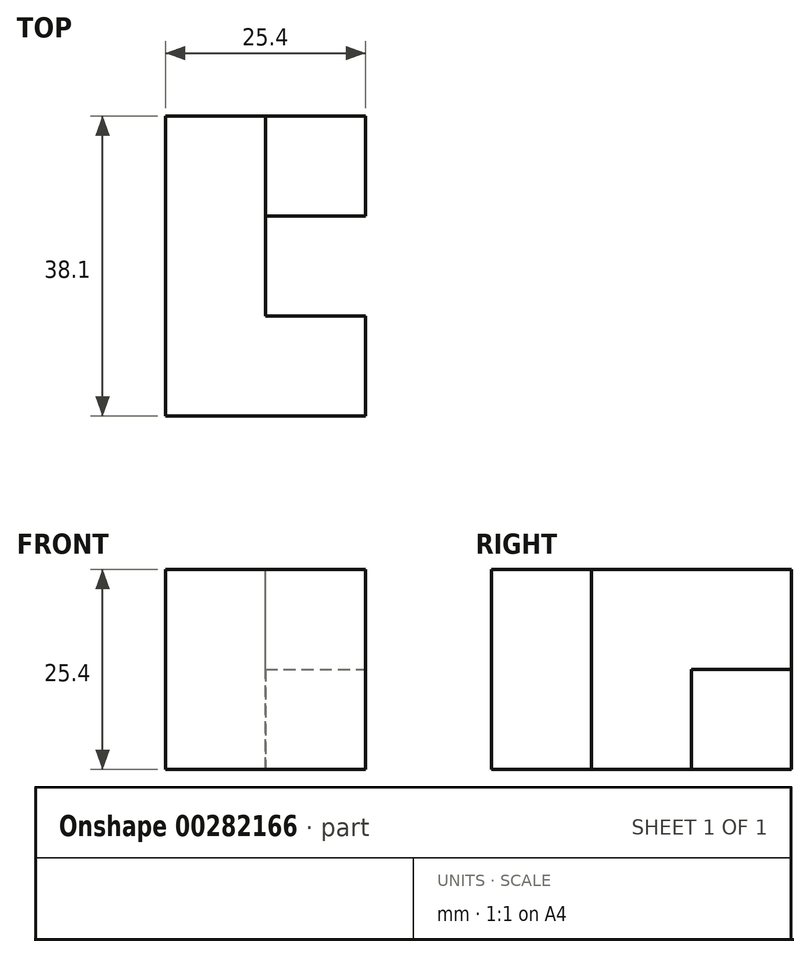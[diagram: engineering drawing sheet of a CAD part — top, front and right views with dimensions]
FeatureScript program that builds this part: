
annotation { "Feature Type Name" : "Feature", "Feature Type Description" : "" }
export const myFeature = defineFeature(function(context is Context, id is Id, definition is map)
    precondition{}
    {
        {
            var Q0;
            Q0=qCreatedBy(makeId("Right.planeOp"),FACE);
            var sketch = newSketch(context, id + "F0", { "sketchPlane" : qUnion([Q0])});
            skLineSegment(sketch, "E0.bottom", {"start": v(0, 0) * mm, "end": v(38.1, 0) * mm});
            skLineSegment(sketch, "E0.top", {"start": v(0, 25.4) * mm, "end": v(38.1, 25.4) * mm});
            skLineSegment(sketch, "E0.left", {"start": v(0, 0) * mm, "end": v(0, 25.4) * mm});
            skLineSegment(sketch, "E0.right", {"start": v(38.1, 0) * mm, "end": v(38.1, 25.4) * mm});
            skSolve(sketch);
        }
        {
            var Q0;
            Q0=makeQuery(id+"F0.imprint","IMPRINT",FACE,{"disambiguationData":[TD([[makeQuery(id+"F0.imprint","IMPRINT",EDGE,{"derivedFrom":sQuery(id+"F0.wireOp",EDGE,"E0.bottom")}),1.0]])]});
            extrude(context, id + "F1", {"entities" : qUnion([Q0]), "depth" : 25.4 * mm});
        }
        {
            var Q0;
            Q0=makeQuery(id+"F1.opExtrude","CAP_FACE",FACE,{"disambiguationData":[OSD([sQuery(id+"F0.wireOp",EDGE,"E0.bottom"),sQuery(id+"F0.wireOp",EDGE,"E0.top"),sQuery(id+"F0.wireOp",EDGE,"E0.left"),sQuery(id+"F0.wireOp",EDGE,"E0.right")])],"isStart":false});
            var sketch = newSketch(context, id + "F2", { "sketchPlane" : qUnion([Q0])});
            skLineSegment(sketch, "E1", {"start": v(25.4, 0) * mm, "end": v(12.7, 0) * mm});
            skLineSegment(sketch, "E2", {"start": v(12.7, 0) * mm, "end": v(12.7, 25.4) * mm});
            skLineSegment(sketch, "E3", {"start": v(12.7, 25.4) * mm, "end": v(38.1, 25.4) * mm});
            skLineSegment(sketch, "E4", {"start": v(38.1, 25.4) * mm, "end": v(38.1, 12.7) * mm});
            skLineSegment(sketch, "E5", {"start": v(38.1, 12.7) * mm, "end": v(25.4, 12.7) * mm});
            skLineSegment(sketch, "E6", {"start": v(25.4, 12.7) * mm, "end": v(25.4, 0) * mm});
            skSolve(sketch);
        }
        {
            var Q0;
            Q0=makeQuery(id+"F2.imprint","IMPRINT",FACE,{"disambiguationData":[TD([[makeQuery(id+"F2.imprint","IMPRINT",EDGE,{"derivedFrom":sQuery(id+"F2.wireOp",EDGE,"E1")}),1.0]])]});
            extrude(context, id + "F3", {"entities" : qUnion([Q0]), "operationType" : NewBodyOperationType.REMOVE, "oppositeDirection" : true, "depth" : 12.7 * mm});
        }
    });
